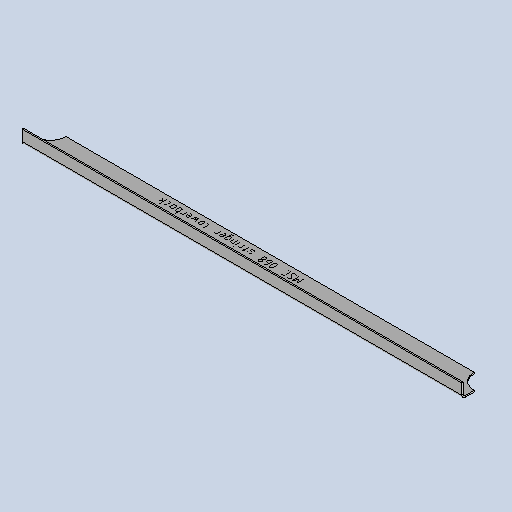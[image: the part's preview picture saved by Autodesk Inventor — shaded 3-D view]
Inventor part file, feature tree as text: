
AUTODESK INVENTOR PART (.ipt)
format: ipt  version: 2025 (Build 290162010, 162A)  size: 345,600 bytes
history: native  units: mm
features: other x5, sketch x5, sheet_metal_op x4, extrude x2, projected_geometry x1
ambient origin geometry x8: Origin, YZ Plane, XZ Plane, XY Plane, X Axis, Y Axis, Z Axis, Center Point
bodies: Solid1 (feature_tree)
feature tree (17):
  sheet_metal_op  "Face1"
  sheet_metal_op  "Flange1"
  extrude  "Extrusion2"  Depth=2.0mm
  other  "Mark2"
  other  "A-Side Definition"
  extrude  "Extrusion4"  Depth=2.0mm
  sketch  "Sketch1"  dims[d1=40.0mm d2=2.0mm]
  other  "Plate1"
  sketch  "Sketch2"  dims[d3=2.0mm d4=1.0mm]
  other  "Plate2"
  sheet_metal_op  "Bend1"
  sheet_metal_op  "Corner1"
  sketch  "Sketch6"  dims[d5=4.0mm]
  sketch  "Sketch9"  dims[d6=2.75mm]
  sketch  "Sketch10"  dims[d7=20.0mm d8=90.0deg d9=2.75mm d10=8.0mm d11=2.0mm d12=2.75mm d24=45.0mm d25=30.0mm d26=0.0mm d40=200.0mm d41=12.0mm d42=5.0mm d43=5.0mm d45=625.0mm d46=45.0mm d47=0.0mm d48=0.0mm]
  projected_geometry  "Projected Loop4"
  other  "Definition1"
